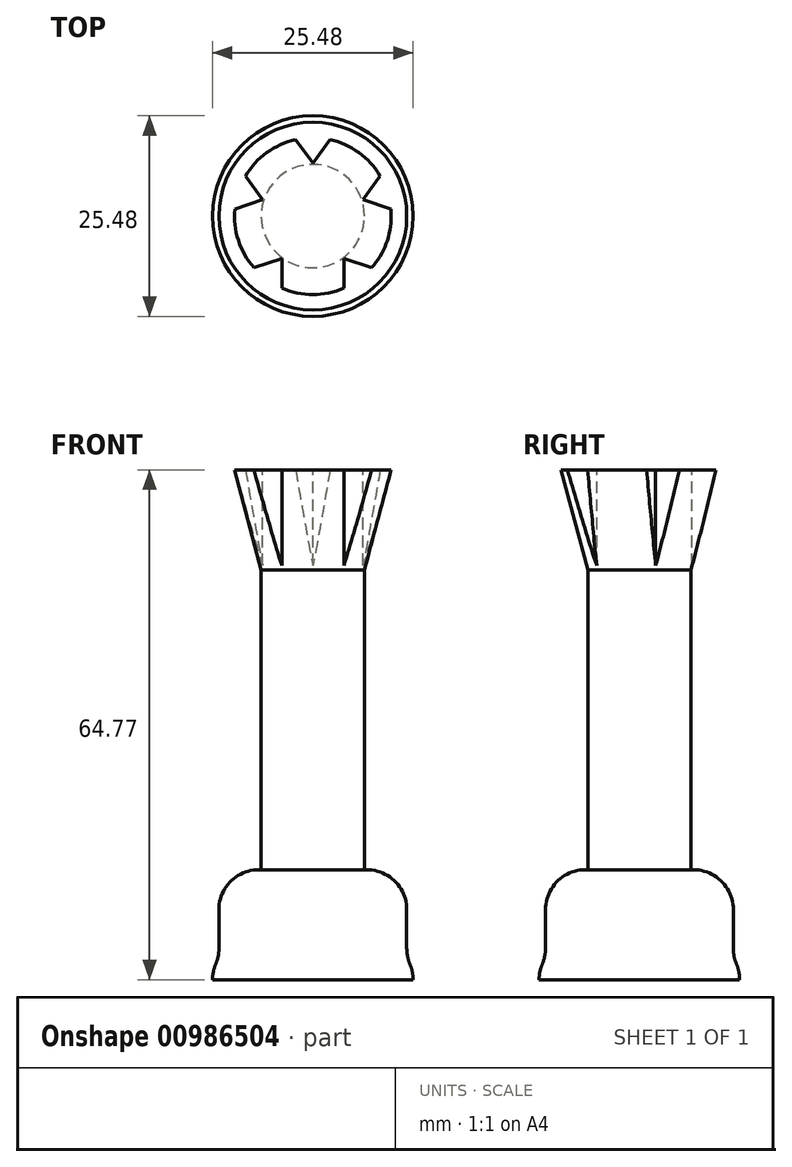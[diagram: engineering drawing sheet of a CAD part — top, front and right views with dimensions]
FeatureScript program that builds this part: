
annotation { "Feature Type Name" : "Feature", "Feature Type Description" : "" }
export const myFeature = defineFeature(function(context is Context, id is Id, definition is map)
    precondition{}
    {
        {
            var Q0;
            Q0=qCreatedBy(makeId("Top.planeOp"),FACE);
            var sketch = newSketch(context, id + "F0", { "sketchPlane" : qUnion([Q0])});
            skCircle(sketch, "E0", {"center": v(0, 0) * mm, "radius": 12.74 * mm});
            skSolve(sketch);
        }
        {
            var Q0;
            Q0 = qSketchRegion(id + "F0", true);
            extrude(context, id + "F1", {"entities" : qUnion([Q0]), "depth" : 5.08 * mm, "offsetDistance" : 25.4 * mm});
        }
        {
            var Q0;
            Q0=makeQuery(id+"F1.opExtrude","CAP_EDGE",EDGE,{"disambiguationData":[OSD([sQuery(id+"F0.wireOp",EDGE,"E0")])],"isStart":false});
            fillet(context, id + "F2", {"entities" : qUnion([Q0]), "radius" : 5.08 * mm, "tangentPropagation" : true, "allowEdgeOverflow" : false});
        }
        {
            var Q0;
            Q0=qCreatedBy(makeId("Top.planeOp"),FACE);
            var sketch = newSketch(context, id + "F3", { "sketchPlane" : qUnion([Q0])});
            skCircle(sketch, "E1", {"center": v(0, 0) * mm, "radius": 11.93 * mm});
            skSolve(sketch);
        }
        {
            var Q0;
            Q0 = qSketchRegion(id + "F3", true);
            extrude(context, id + "F4", {"entities" : qUnion([Q0]), "operationType" : NewBodyOperationType.ADD, "depth" : 13.97 * mm, "offsetDistance" : 25.4 * mm});
        }
        {
            var Q0;
            Q0=makeQuery(id+"F4.opExtrude","SWEPT_FACE",FACE,{"disambiguationData":[OSD([sQuery(id+"F3.wireOp",EDGE,"E1")])]});
            fillet(context, id + "F5", {"entities" : qUnion([Q0]), "radius" : 5.08 * mm, "tangentPropagation" : true, "allowEdgeOverflow" : false});
        }
        {
            var Q0;
            Q0=qCreatedBy(makeId("Top.planeOp"),FACE);
            var sketch = newSketch(context, id + "F6", { "sketchPlane" : qUnion([Q0])});
            skCircle(sketch, "E2", {"center": v(0, 0) * mm, "radius": 6.55 * mm});
            skSolve(sketch);
        }
        {
            var Q0;
            Q0 = qSketchRegion(id + "F6", true);
            extrude(context, id + "F7", {"entities" : qUnion([Q0]), "operationType" : NewBodyOperationType.ADD, "depth" : 24.13 * mm, "offsetDistance" : 25.4 * mm});
        }
        {
            var Q0;
            Q0=makeQuery(id+"F7.opExtrude","CAP_FACE",FACE,{"disambiguationData":[OSD([sQuery(id+"F6.wireOp",EDGE,"E2")])],"isStart":false});
            extrude(context, id + "F8", {"entities" : qUnion([Q0]), "operationType" : NewBodyOperationType.ADD, "depth" : 27.94 * mm, "offsetDistance" : 25.4 * mm});
        }
        {
            var Q0;
            Q0=makeQuery(id+"F8.opExtrude","CAP_FACE",FACE,{"disambiguationData":[OSD([sQuery(id+"F6.wireOp",EDGE,"E2")])],"isStart":false});
            extrude(context, id + "F9", {"entities" : qUnion([Q0]), "operationType" : NewBodyOperationType.ADD, "depth" : 12.7 * mm, "offsetDistance" : 25.4 * mm, "hasDraft" : true, "draftAngle" : 15 * degree});
        }
        {
            var Q0;
            Q0=makeQuery(id+"F9.opExtrude","CAP_FACE",FACE,{"disambiguationData":[OSD([sQuery(id+"F6.wireOp",EDGE,"E2")])],"isStart":false});
            var sketch = newSketch(context, id + "F10", { "sketchPlane" : qUnion([Q0])});
            skLineSegment(sketch, "E3.bottom", {"start": v(-3.94, -13.56) * mm, "end": v(3.94, -13.56) * mm});
            skLineSegment(sketch, "E3.top", {"start": v(-3.94, 55.17) * mm, "end": v(3.94, 55.17) * mm});
            skLineSegment(sketch, "E3.left", {"start": v(-3.94, -13.56) * mm, "end": v(-3.94, 55.17) * mm});
            skLineSegment(sketch, "E3.right", {"start": v(3.94, -13.56) * mm, "end": v(3.94, 55.17) * mm});
            skPoint(sketch, "E3.middle", {"position": v(0, 20.8) * mm});
            skLineSegment(sketch, "E4.1.0", {"start": v(11.68, -7.94) * mm, "end": v(-53.69, 13.3) * mm});
            skLineSegment(sketch, "E4.1.1", {"start": v(-53.69, 13.3) * mm, "end": v(-51.25, 20.8) * mm});
            skLineSegment(sketch, "E4.1.2", {"start": v(14.12, -0.45) * mm, "end": v(-51.25, 20.8) * mm});
            skLineSegment(sketch, "E4.1.3", {"start": v(11.68, -7.94) * mm, "end": v(14.12, -0.45) * mm});
            skLineSegment(sketch, "E4.2.0", {"start": v(11.16, 8.66) * mm, "end": v(-29.24, -46.95) * mm});
            skLineSegment(sketch, "E4.2.1", {"start": v(-29.24, -46.95) * mm, "end": v(-35.61, -42.32) * mm});
            skLineSegment(sketch, "E4.2.2", {"start": v(4.79, 13.29) * mm, "end": v(-35.61, -42.32) * mm});
            skLineSegment(sketch, "E4.2.3", {"start": v(11.16, 8.66) * mm, "end": v(4.79, 13.29) * mm});
            skLineSegment(sketch, "E4.3.0", {"start": v(-4.79, 13.29) * mm, "end": v(35.61, -42.32) * mm});
            skLineSegment(sketch, "E4.3.1", {"start": v(35.61, -42.32) * mm, "end": v(29.24, -46.95) * mm});
            skLineSegment(sketch, "E4.3.2", {"start": v(-11.16, 8.66) * mm, "end": v(29.24, -46.95) * mm});
            skLineSegment(sketch, "E4.3.3", {"start": v(-4.79, 13.29) * mm, "end": v(-11.16, 8.66) * mm});
            skLineSegment(sketch, "E4.4.0", {"start": v(-14.12, -0.45) * mm, "end": v(51.25, 20.8) * mm});
            skLineSegment(sketch, "E4.4.1", {"start": v(51.25, 20.8) * mm, "end": v(53.69, 13.3) * mm});
            skLineSegment(sketch, "E4.4.2", {"start": v(-11.68, -7.94) * mm, "end": v(53.69, 13.3) * mm});
            skLineSegment(sketch, "E4.4.3", {"start": v(-14.12, -0.45) * mm, "end": v(-11.68, -7.94) * mm});
            skPoint(sketch, "E4.center", {"position": v(0, 0) * mm});
            skSolve(sketch);
        }
        {
            var Q0;
            {var subQ0=sQuery(id+"F10.wireOp",EDGE,"E4.1.0");var subQ1=sQuery(id+"F10.wireOp",EDGE,"E3.right");var subQ2=makeQuery(id+"F10.imprint","INTERSECT",VERTEX,{"derivedFrom":[subQ1,subQ0]});Q0=makeQuery(id+"F10.imprint","IMPRINT",FACE,{"disambiguationData":[TD([[makeQuery(id+"F10.imprint","IMPRINT",EDGE,{"disambiguationData":[TD([[subQ2,1.0]])],"derivedFrom":subQ1}),-1.0]])]});}
            var Q1;
            {var subQ0=sQuery(id+"F10.wireOp",EDGE,"E4.2.0");var subQ1=sQuery(id+"F10.wireOp",EDGE,"E4.1.2");var subQ2=makeQuery(id+"F10.imprint","INTERSECT",VERTEX,{"derivedFrom":[subQ1,subQ0]});Q1=makeQuery(id+"F10.imprint","IMPRINT",FACE,{"disambiguationData":[TD([[makeQuery(id+"F10.imprint","IMPRINT",EDGE,{"disambiguationData":[TD([[subQ2,1.0]])],"derivedFrom":subQ1}),-1.0]])]});}
            var Q2;
            {var subQ0=sQuery(id+"F10.wireOp",EDGE,"E4.3.0");var subQ1=sQuery(id+"F10.wireOp",EDGE,"E4.2.2");var subQ2=makeQuery(id+"F10.imprint","INTERSECT",VERTEX,{"derivedFrom":[subQ1,subQ0]});Q2=makeQuery(id+"F10.imprint","IMPRINT",FACE,{"disambiguationData":[TD([[makeQuery(id+"F10.imprint","IMPRINT",EDGE,{"disambiguationData":[TD([[subQ2,1.0]])],"derivedFrom":subQ1}),-1.0]])]});}
            var Q3;
            {var subQ0=sQuery(id+"F10.wireOp",EDGE,"E4.4.0");var subQ1=sQuery(id+"F10.wireOp",EDGE,"E4.3.2");var subQ2=makeQuery(id+"F10.imprint","INTERSECT",VERTEX,{"derivedFrom":[subQ1,subQ0]});Q3=makeQuery(id+"F10.imprint","IMPRINT",FACE,{"disambiguationData":[TD([[makeQuery(id+"F10.imprint","IMPRINT",EDGE,{"disambiguationData":[TD([[subQ2,1.0]])],"derivedFrom":subQ1}),-1.0]])]});}
            var Q4;
            {var subQ0=sQuery(id+"F10.wireOp",EDGE,"E4.4.2");var subQ1=sQuery(id+"F10.wireOp",EDGE,"E3.left");var subQ2=makeQuery(id+"F10.imprint","INTERSECT",VERTEX,{"derivedFrom":[subQ1,subQ0]});Q4=makeQuery(id+"F10.imprint","IMPRINT",FACE,{"disambiguationData":[TD([[makeQuery(id+"F10.imprint","IMPRINT",EDGE,{"disambiguationData":[TD([[subQ2,1.0]])],"derivedFrom":subQ1}),1.0]])]});}
            extrude(context, id + "F11", {"entities" : qUnion([Q0, Q1, Q2, Q3, Q4]), "operationType" : NewBodyOperationType.REMOVE, "oppositeDirection" : true, "depth" : 25.4 * mm, "offsetDistance" : 25.4 * mm});
        }
    });
